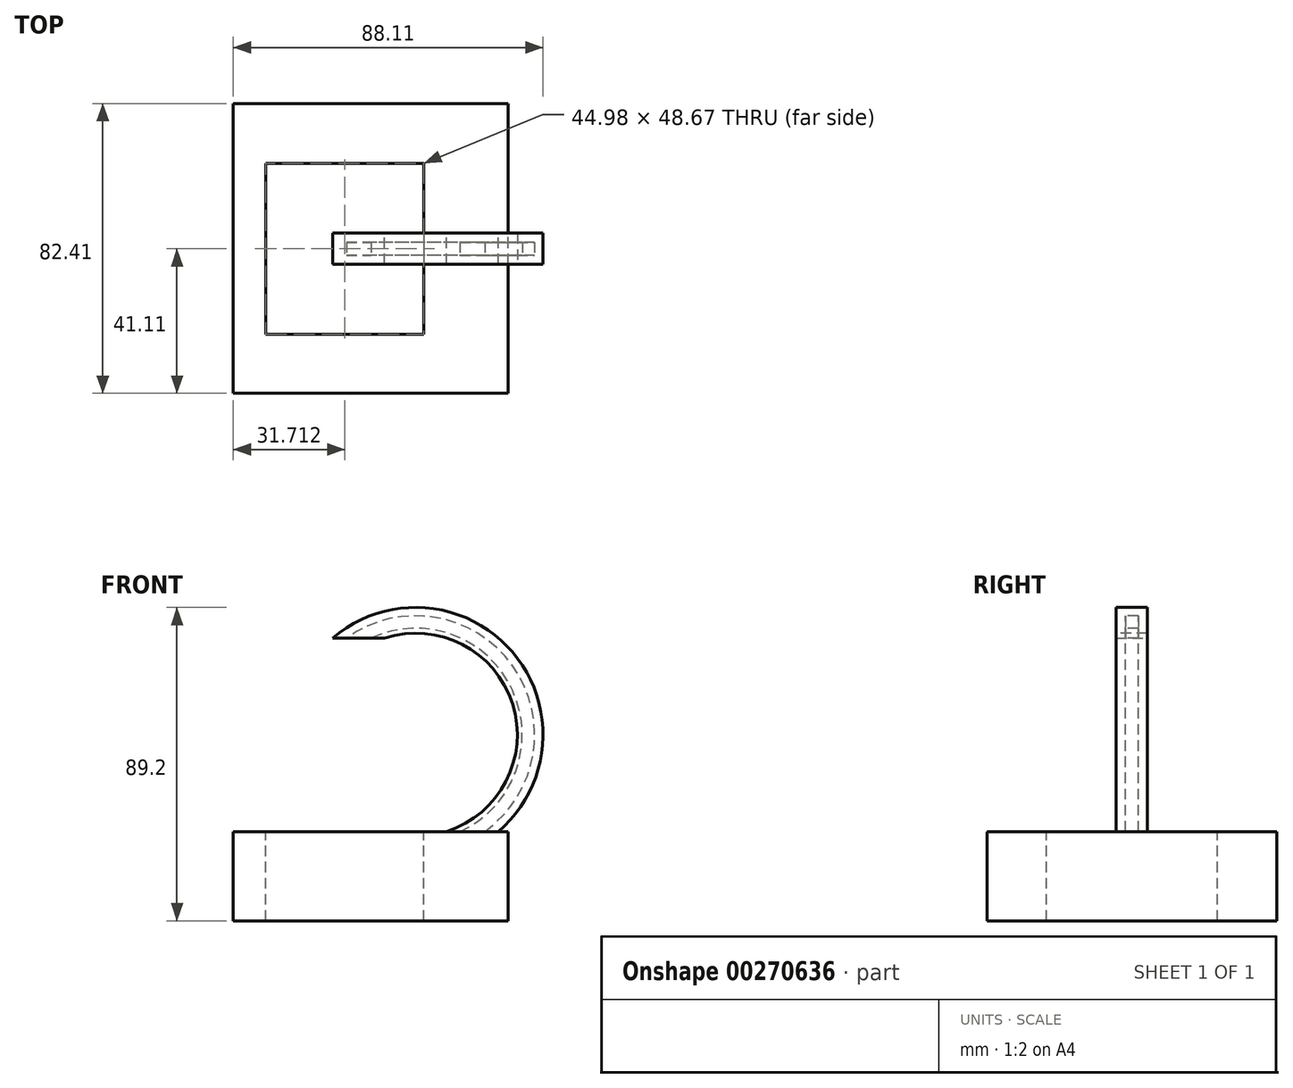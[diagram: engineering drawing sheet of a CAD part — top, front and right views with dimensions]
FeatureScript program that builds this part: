
annotation { "Feature Type Name" : "Feature", "Feature Type Description" : "" }
export const myFeature = defineFeature(function(context is Context, id is Id, definition is map)
    precondition{}
    {
        {
            var Q0;
            Q0=qCreatedBy(makeId("Top.planeOp"),FACE);
            var sketch = newSketch(context, id + "F0", { "sketchPlane" : qUnion([Q0])});
            skLineSegment(sketch, "E0.bottom", {"start": v(7.37, -4.42) * mm, "end": v(-7.37, -4.42) * mm});
            skLineSegment(sketch, "E0.top", {"start": v(7.37, 4.42) * mm, "end": v(-7.37, 4.42) * mm});
            skLineSegment(sketch, "E0.left", {"start": v(7.37, -4.42) * mm, "end": v(7.37, 4.42) * mm});
            skLineSegment(sketch, "E0.right", {"start": v(-7.37, -4.42) * mm, "end": v(-7.37, 4.42) * mm});
            skPoint(sketch, "E0.middle", {"position": v(0, 0) * mm});
            skLineSegment(sketch, "E1.bottom", {"start": v(3.5, 1.84) * mm, "end": v(-3.5, 1.84) * mm});
            skLineSegment(sketch, "E1.top", {"start": v(3.5, -1.84) * mm, "end": v(-3.5, -1.84) * mm});
            skLineSegment(sketch, "E1.left", {"start": v(3.5, 1.84) * mm, "end": v(3.5, -1.84) * mm});
            skLineSegment(sketch, "E1.right", {"start": v(-3.5, 1.84) * mm, "end": v(-3.5, -1.84) * mm});
            skSolve(sketch);
        }
        {
            var Q0;
            Q0=qCreatedBy(makeId("Front.planeOp"),FACE);
            var sketch = newSketch(context, id + "F1", { "sketchPlane" : qUnion([Q0])});
            skLineSegment(sketch, "E2", {"start": v(0, 0) * mm, "end": v(0, 27.56) * mm});
            skArc(sketch, "E3", {"start": v(0, 27.56) * mm, "mid": v(-16.17, 43.73) * mm, "end": v(-32.34, 27.56) * mm});
            skSolve(sketch);
        }
        {
            var Q0;
            Q0=makeQuery(id+"F0.imprint","IMPRINT",FACE,{"disambiguationData":[TD([[makeQuery(id+"F0.imprint","IMPRINT",EDGE,{"derivedFrom":sQuery(id+"F0.wireOp",EDGE,"E0.bottom")}),-1.0]])]});
            var Q1;
            Q1=sQuery(id+"F1.wireOp",EDGE,"E3");
            sweep(context, id + "F2", {"profiles" : qUnion([Q0]), "path" : qUnion([Q1])});
        }
        {
            var Q0;
            Q0=qCreatedBy(makeId("Top.planeOp"),FACE);
            var sketch = newSketch(context, id + "F3", { "sketchPlane" : qUnion([Q0])});
            skLineSegment(sketch, "E4.bottom", {"start": v(10.14, -41.11) * mm, "end": v(-68.03, -41.11) * mm});
            skLineSegment(sketch, "E4.top", {"start": v(10.14, 41.3) * mm, "end": v(-68.03, 41.3) * mm});
            skLineSegment(sketch, "E4.left", {"start": v(10.14, -41.11) * mm, "end": v(10.14, 41.3) * mm});
            skLineSegment(sketch, "E4.right", {"start": v(-68.03, -41.11) * mm, "end": v(-68.03, 41.3) * mm});
            skLineSegment(sketch, "E5.bottom", {"start": v(-13.83, 24.33) * mm, "end": v(-58.8, 24.33) * mm});
            skLineSegment(sketch, "E5.top", {"start": v(-13.83, -24.33) * mm, "end": v(-58.8, -24.33) * mm});
            skLineSegment(sketch, "E5.left", {"start": v(-13.83, 24.33) * mm, "end": v(-13.83, -24.33) * mm});
            skLineSegment(sketch, "E5.right", {"start": v(-58.8, 24.33) * mm, "end": v(-58.8, -24.33) * mm});
            skPoint(sketch, "E5.middle", {"position": v(-36.32, 0) * mm});
            skSolve(sketch);
        }
        {
            var Q0;
            Q0=makeQuery(id+"F3.imprint","IMPRINT",FACE,{"disambiguationData":[TD([[makeQuery(id+"F3.imprint","IMPRINT",EDGE,{"derivedFrom":sQuery(id+"F3.wireOp",EDGE,"E4.bottom")}),-1.0]])]});
            extrude(context, id + "F4", {"entities" : qUnion([Q0]), "operationType" : NewBodyOperationType.ADD, "oppositeDirection" : true, "depth" : 25.4 * mm});
        }
        {
            var Q0;
            Q0=makeQuery(id+"F3.imprint","IMPRINT",FACE,{"disambiguationData":[TD([[makeQuery(id+"F3.imprint","IMPRINT",EDGE,{"derivedFrom":sQuery(id+"F3.wireOp",EDGE,"E5.bottom")}),1.0]])]});
            extrude(context, id + "F5", {"entities" : qUnion([Q0]), "operationType" : NewBodyOperationType.REMOVE, "oppositeDirection" : true, "depth" : 2.54 * mm});
        }
    });
